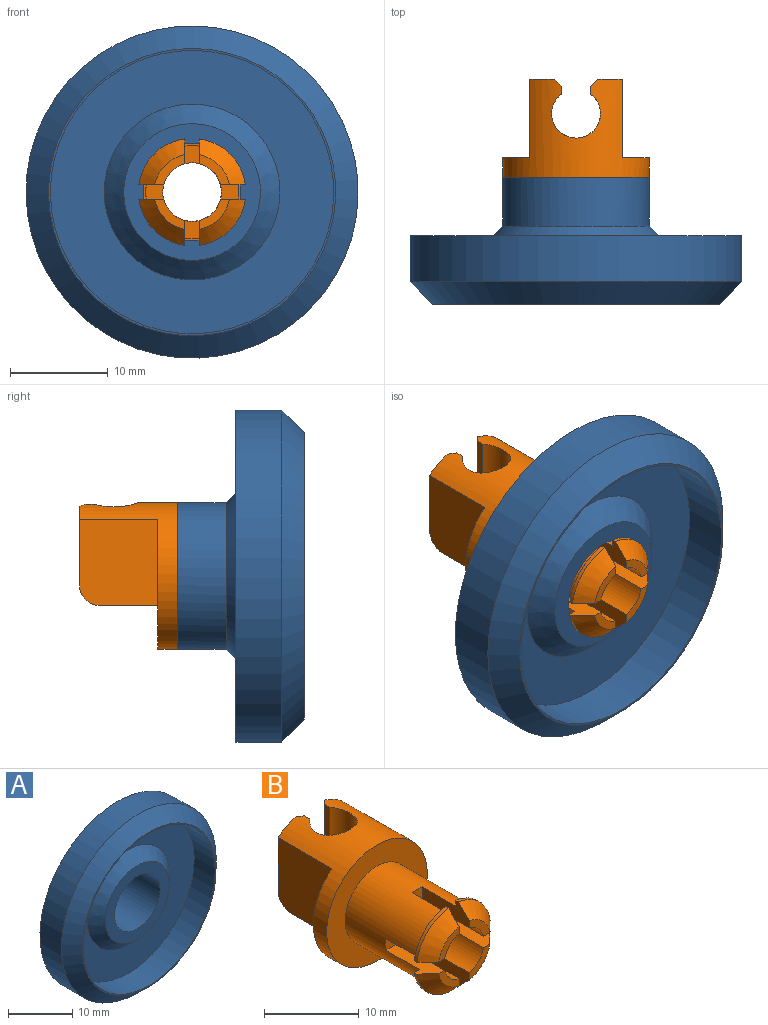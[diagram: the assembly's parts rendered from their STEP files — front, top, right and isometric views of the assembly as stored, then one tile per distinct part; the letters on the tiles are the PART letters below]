
ASSEMBLY  parts=2 mates=1
PART A: 12 faces, bbox 34x13x34 mm
  f0: cylinder r=17mm len=34mm, axis (0,1,0), area 502mm2, adj f2,f9
  f1: plane 29.4x29.4mm, normal (0,-1,0), area 18.3mm2, adj f3,f9
  f2: plane 34x34mm, normal (0,1,0), area 680.9mm2, adj f0,f11
  f3: cylinder r=14.5mm len=29mm, axis (0,-1,0), area 419.1mm2, adj f1,f4
  f4: plane 29x29mm, normal (0,-1,0), area 406.1mm2, adj f3,f10
  f5: cylinder r=7.5mm len=15mm, axis (0,-1,0), area 235.6mm2, adj f6,f11
  f6: plane 15x15mm, normal (0,1,0), area 98.2mm2, adj f5,f8
  f7: plane 14x14mm, normal (0,-1,0), area 75.4mm2, adj f8,f10
  f8: cylinder r=5mm len=10.4mm, axis (0,-1,0), area 326.7mm2, adj f6,f7
  f9: cone r=14.7mm half-angle=45deg, axis (0,1,0), area 323.9mm2, adj f0,f1
  f10: cone r=7mm half-angle=45deg, axis (0,1,0), area 142.2mm2, adj f4,f7
  f11: cone r=7.5mm half-angle=45deg, axis (0,-1,0), area 71.1mm2, adj f2,f5
PART B: 54 faces, bbox 15x23x15 mm
  f0: cylinder r=3mm len=3.5mm, axis (0,1,0), area 8.8mm2, adj f5,f26,f27,f30,f46,f51
  f1: cylinder r=3mm len=15mm, axis (0,1,0), area 240.3mm2, adj f2,f3,f4,f11,f12,f13,f14,f22
  f2: plane 1.85x1.5mm, normal (0,-1,0), area 2.6mm2, adj f1,f10,f34,f35
  f3: plane 1.85x1.5mm, normal (0,-1,0), area 2.6mm2, adj f1,f10,f36,f37
  f4: plane 1.85x1.5mm, normal (0,-1,0), area 2.6mm2, adj f1,f10,f38,f39
  f5: plane 8.17x2.55mm, normal (0,1,0), area 17.4mm2, adj f0,f19,f24,f30,f46,f48
  f6: plane 6x1.75mm, normal (0,0,-1), area 10.5mm2, adj f22,f24,f46,f48
  f7: cylinder r=5.5mm len=4.7mm, axis (0,1,0), area 2.9mm2, adj f16,f35,f36,f43
  f8: cylinder r=5.5mm len=4.7mm, axis (0,1,0), area 2.9mm2, adj f17,f37,f38,f42
  f9: cylinder r=5.5mm len=4.7mm, axis (0,1,0), area 2.9mm2, adj f18,f39,f40,f41
  f10: cylinder r=4.75mm len=11mm, axis (0,1,0), area 298.2mm2, adj f2,f3,f4,f15,f16,f17,f18,f21
  f11: plane 3.08x3.08mm, normal (0,-1,0), area 3.5mm2, adj f1,f33,f34,f44
  f12: plane 3.08x3.08mm, normal (0,-1,0), area 3.5mm2, adj f1,f35,f36,f43
  f13: plane 3.08x3.08mm, normal (0,-1,0), area 3.5mm2, adj f1,f37,f38,f42
  f14: plane 3.08x3.08mm, normal (0,-1,0), area 3.5mm2, adj f1,f39,f40,f41
  f15: plane 4.7x4.7mm, normal (0,1,0), area 4.9mm2, adj f10,f31,f33,f34
  f16: plane 4.7x4.7mm, normal (0,1,0), area 4.9mm2, adj f7,f10,f35,f36
  f17: plane 4.7x4.7mm, normal (0,1,0), area 4.9mm2, adj f8,f10,f37,f38
  f18: plane 4.7x4.7mm, normal (0,1,0), area 4.9mm2, adj f9,f10,f39,f40
  f19: cylinder r=7.5mm len=15mm, axis (0,1,0), area 152.6mm2, adj f5,f20,f21,f22,f24,f25,f26,f27
  f20: plane 8.17x2.55mm, normal (0,1,0), area 17.4mm2, adj f19,f25,f29,f45,f47,f49
  f21: plane 15x15mm, normal (0,-1,0), area 105.8mm2, adj f10,f19
  f22: plane 15x13.3mm, normal (0,1,0), area 85.9mm2, adj f1,f6,f19,f23,f24,f25,f46,f47
  f23: plane 6x1.75mm, normal (0,0,-1), area 10.5mm2, adj f22,f25,f47,f49
  f24: plane 8.8x8mm, normal (-1,0,0), area 69.6mm2, adj f5,f6,f19,f22,f48
  f25: plane 8.8x8mm, normal (1,0,0), area 69.6mm2, adj f19,f20,f22,f23,f49
  f26: plane 4.75x0.8mm, normal (1,0,0), area 3.8mm2, adj f0,f19,f27,f30
  f27: cylinder r=2.5mm len=5.84mm, axis (0,0,1), area 44.4mm2, adj f0,f19,f26,f28,f45,f50,f51,f52
  f28: plane 4.75x0.8mm, normal (-1,0,0), area 3.8mm2, adj f19,f27,f29,f45
  f29: plane 5.35x0.74mm, normal (-0.71,0.71,0), area 4.9mm2, adj f19,f20,f28,f45
  f30: plane 5.35x0.74mm, normal (0.71,0.71,0), area 4.9mm2, adj f0,f5,f19,f26
  f31: cylinder r=5.5mm len=4.7mm, axis (0,1,0), area 2.9mm2, adj f15,f33,f34,f44
  f32: plane 1.85x1.5mm, normal (0,-1,0), area 2.6mm2, adj f1,f10,f33,f40
  f33: plane 7.05x2.59mm, normal (-1,0,0), area 12.7mm2, adj f1,f10,f11,f15,f31,f32,f44
  f34: plane 7.05x2.59mm, normal (0,0,1), area 12.7mm2, adj f1,f2,f10,f11,f15,f31,f44
  f35: plane 7.05x2.59mm, normal (0,0,-1), area 12.7mm2, adj f1,f2,f7,f10,f12,f16,f43
  f36: plane 7.05x2.59mm, normal (-1,0,0), area 12.7mm2, adj f1,f3,f7,f10,f12,f16,f43
  f37: plane 7.05x2.59mm, normal (1,0,0), area 12.7mm2, adj f1,f3,f8,f10,f13,f17,f42
  f38: plane 7.05x2.59mm, normal (0,0,-1), area 12.7mm2, adj f1,f4,f8,f10,f13,f17,f42
  f39: plane 7.05x2.59mm, normal (0,0,1), area 12.7mm2, adj f1,f4,f9,f10,f14,f18,f41
  f40: plane 7.05x2.59mm, normal (1,0,0), area 12.7mm2, adj f1,f9,f10,f14,f18,f32,f41
  f41: cone r=3.9mm half-angle=45deg, axis (0,1,0), area 13.2mm2, adj f9,f14,f39,f40
  f42: cone r=3.9mm half-angle=45deg, axis (0,1,0), area 13.2mm2, adj f8,f13,f37,f38
  f43: cone r=3.9mm half-angle=45deg, axis (0,1,0), area 13.2mm2, adj f7,f12,f35,f36
  f44: cone r=3.9mm half-angle=45deg, axis (0,1,0), area 13.2mm2, adj f11,f31,f33,f34
  f45: cylinder r=3mm len=3.5mm, axis (0,1,0), area 8.8mm2, adj f20,f27,f28,f29,f47,f52
  f46: plane 8x7mm, normal (1,0,0), area 41.1mm2, adj f0,f5,f6,f22,f48,f50,f51,f53
  f47: plane 8x7mm, normal (-1,0,0), area 41.1mm2, adj f20,f22,f23,f45,f49,f50,f52,f53
  f48: cylinder r=2mm len=2mm, axis (1,0,0), area 5.5mm2, adj f5,f6,f24,f46
  f49: cylinder r=2mm len=2mm, axis (1,0,0), area 5.5mm2, adj f20,f23,f25,f47
  f50: cylinder r=5mm len=6mm, axis (0,-1,0), area 18.8mm2, adj f27,f46,f47,f51,f52,f53
  f51: plane 4.33x0.5mm, normal (0,-1,0), area 1.5mm2, adj f0,f27,f46,f50
  f52: plane 4.33x0.5mm, normal (0,-1,0), area 1.5mm2, adj f27,f45,f47,f50
  f53: plane 6x5mm, normal (0,1,0), area 14mm2, adj f1,f46,f47,f50
PLACE A rot(axis=(0,1,0),117.5deg) t=(-3.71,-5.79,1.27)mm
PLACE B t=(-3.71,2.21,1.27)mm fixed
MATE revolute A.f8 <-> B.f19  axis (0,1,0) through (-3.71,0.21,1.27)mm
